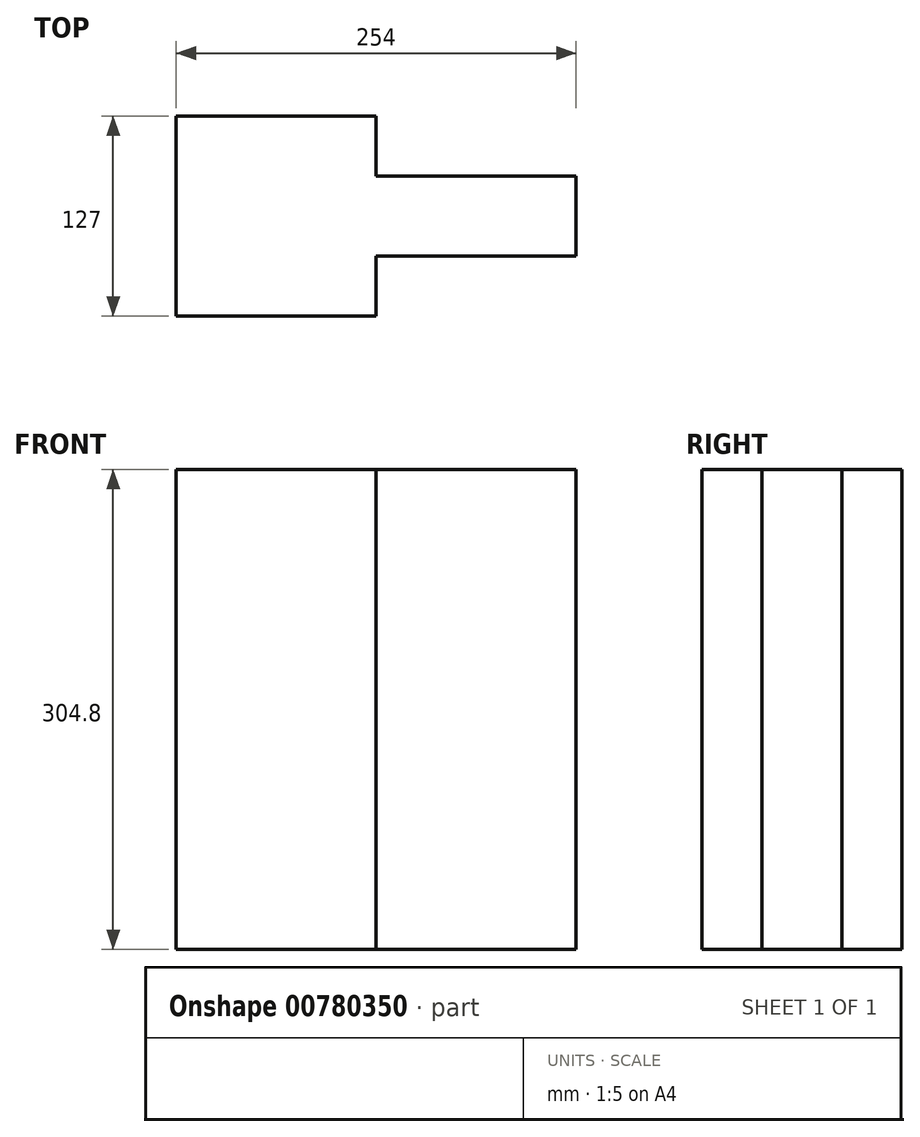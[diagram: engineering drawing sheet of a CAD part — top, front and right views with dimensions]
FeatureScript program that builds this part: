
annotation { "Feature Type Name" : "Feature", "Feature Type Description" : "" }
export const myFeature = defineFeature(function(context is Context, id is Id, definition is map)
    precondition{}
    {
        {
            var Q0;
            Q0=qCreatedBy(makeId("Front.planeOp"),FACE);
            var sketch = newSketch(context, id + "F0", { "sketchPlane" : qUnion([Q0])});
            skLineSegment(sketch, "E0.bottom", {"start": v(-88.88, 181.86) * mm, "end": v(38.12, 181.86) * mm});
            skLineSegment(sketch, "E0.top", {"start": v(-88.88, -122.94) * mm, "end": v(38.12, -122.94) * mm});
            skLineSegment(sketch, "E0.left", {"start": v(-88.88, 181.86) * mm, "end": v(-88.88, -122.94) * mm});
            skLineSegment(sketch, "E0.right", {"start": v(38.12, 181.86) * mm, "end": v(38.12, -122.94) * mm});
            skLineSegment(sketch, "E1.bottom", {"start": v(38.12, 181.86) * mm, "end": v(165.12, 181.86) * mm});
            skLineSegment(sketch, "E1.top", {"start": v(38.12, -122.94) * mm, "end": v(165.12, -122.94) * mm});
            skLineSegment(sketch, "E1.right", {"start": v(165.12, 181.86) * mm, "end": v(165.12, -122.94) * mm});
            skSolve(sketch);
        }
        {
            var Q0;
            Q0=makeQuery(id+"F0.imprint","IMPRINT",FACE,{"disambiguationData":[TD([[makeQuery(id+"F0.imprint","IMPRINT",EDGE,{"derivedFrom":sQuery(id+"F0.wireOp",EDGE,"E0.bottom")}),-1.0]])]});
            extrude(context, id + "F1", {"entities" : qUnion([Q0]), "endBound" : BoundingType.SYMMETRIC, "depth" : 127 * mm, "offsetDistance" : 25.4 * mm});
        }
        {
            var Q0;
            Q0=makeQuery(id+"F0.imprint","IMPRINT",FACE,{"disambiguationData":[TD([[makeQuery(id+"F0.imprint","IMPRINT",EDGE,{"derivedFrom":sQuery(id+"F0.wireOp",EDGE,"E1.bottom")}),-1.0]])]});
            extrude(context, id + "F2", {"entities" : qUnion([Q0]), "operationType" : NewBodyOperationType.ADD, "endBound" : BoundingType.SYMMETRIC, "depth" : 50.8 * mm, "offsetDistance" : 25.4 * mm});
        }
    });
